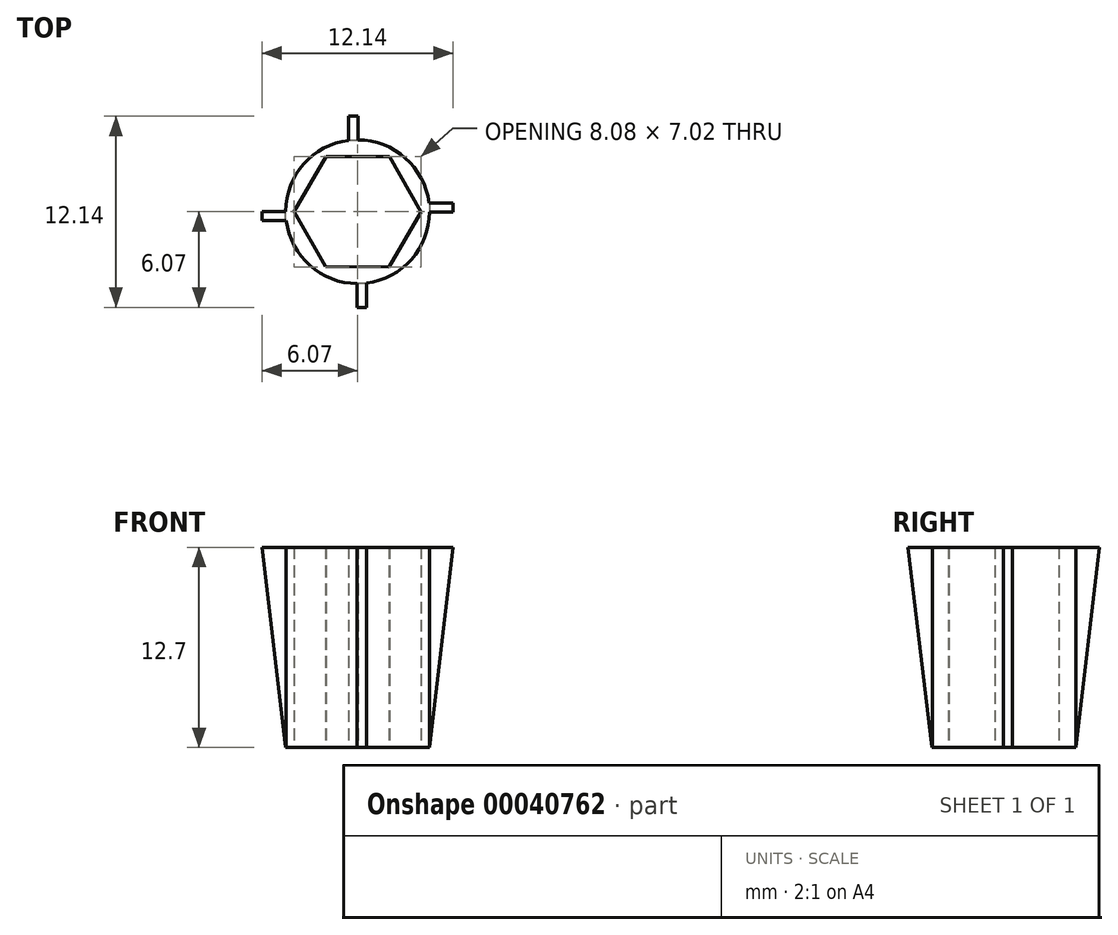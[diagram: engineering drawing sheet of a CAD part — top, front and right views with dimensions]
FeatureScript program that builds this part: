
annotation { "Feature Type Name" : "Feature", "Feature Type Description" : "" }
export const myFeature = defineFeature(function(context is Context, id is Id, definition is map)
    precondition{}
    {
        {
            var Q0;
            Q0=qCreatedBy(makeId("Top.planeOp"),FACE);
            var sketch = newSketch(context, id + "F0", { "sketchPlane" : qUnion([Q0])});
            skCircle(sketch, "E0.cCircle", {"center": v(0, 0) * mm, "radius": 3.5 * mm, "construction": true});
            skLineSegment(sketch, "E0.0", {"start": v(2.04, 3.5) * mm, "end": v(4.04, -0.02) * mm});
            skLineSegment(sketch, "E0.1", {"start": v(4.04, -0.02) * mm, "end": v(2, -3.5) * mm});
            skLineSegment(sketch, "E0.2", {"start": v(2, -3.5) * mm, "end": v(-2.04, -3.5) * mm});
            skLineSegment(sketch, "E0.3", {"start": v(-2.04, -3.5) * mm, "end": v(-4.04, 0.02) * mm});
            skLineSegment(sketch, "E0.4", {"start": v(-4.04, 0.02) * mm, "end": v(-2, 3.5) * mm});
            skLineSegment(sketch, "E0.5", {"start": v(-2, 3.5) * mm, "end": v(2.04, 3.5) * mm});
            skPoint(sketch, "E0.0.midPoint", {"position": v(3.04, 1.74) * mm});
            skLineSegment(sketch, "E1", {"start": v(-2, 3.5) * mm, "end": v(-2.04, -3.5) * mm, "construction": true});
            skCircle(sketch, "E2", {"center": v(0, 0) * mm, "radius": 4.57 * mm});
            skLineSegment(sketch, "E3.bottom", {"start": v(4.04, -0.02) * mm, "end": v(6.07, -0.02) * mm});
            skLineSegment(sketch, "E3.top", {"start": v(4.04, 0.56) * mm, "end": v(6.07, 0.56) * mm});
            skLineSegment(sketch, "E3.left", {"start": v(4.04, -0.02) * mm, "end": v(4.04, 0.56) * mm});
            skLineSegment(sketch, "E3.right", {"start": v(6.07, -0.02) * mm, "end": v(6.07, 0.56) * mm});
            skLineSegment(sketch, "E4.1.0", {"start": v(-0.56, 4.04) * mm, "end": v(-0.56, 6.07) * mm});
            skLineSegment(sketch, "E4.1.1", {"start": v(0.02, 6.07) * mm, "end": v(-0.56, 6.07) * mm});
            skLineSegment(sketch, "E4.1.2", {"start": v(0.02, 4.04) * mm, "end": v(0.02, 6.07) * mm});
            skLineSegment(sketch, "E4.1.3", {"start": v(0.02, 4.04) * mm, "end": v(-0.56, 4.04) * mm});
            skLineSegment(sketch, "E4.2.0", {"start": v(-4.04, -0.56) * mm, "end": v(-6.07, -0.56) * mm});
            skLineSegment(sketch, "E4.2.1", {"start": v(-6.07, 0.02) * mm, "end": v(-6.07, -0.56) * mm});
            skLineSegment(sketch, "E4.2.2", {"start": v(-4.04, 0.02) * mm, "end": v(-6.07, 0.02) * mm});
            skLineSegment(sketch, "E4.2.3", {"start": v(-4.04, 0.02) * mm, "end": v(-4.04, -0.56) * mm});
            skLineSegment(sketch, "E4.3.0", {"start": v(0.56, -4.04) * mm, "end": v(0.56, -6.07) * mm});
            skLineSegment(sketch, "E4.3.1", {"start": v(-0.02, -6.07) * mm, "end": v(0.56, -6.07) * mm});
            skLineSegment(sketch, "E4.3.2", {"start": v(-0.02, -4.04) * mm, "end": v(-0.02, -6.07) * mm});
            skLineSegment(sketch, "E4.3.3", {"start": v(-0.02, -4.04) * mm, "end": v(0.56, -4.04) * mm});
            skSolve(sketch);
        }
        {
            var Q0;
            Q0=makeQuery(id+"F0.imprint","IMPRINT",FACE,{"disambiguationData":[TD([[makeQuery(id+"F0.imprint","IMPRINT",EDGE,{"derivedFrom":sQuery(id+"F0.wireOp",EDGE,"E0.0")}),1.0]])]});
            var Q1;
            {var subQ0=sQuery(id+"F0.wireOp",EDGE,"E3.right");Q1=makeQuery(id+"F0.imprint","IMPRINT",FACE,{"disambiguationData":[TD([[makeQuery(id+"F0.imprint","IMPRINT",EDGE,{"derivedFrom":subQ0}),1.0]])]});}
            var Q2;
            {var subQ0=sQuery(id+"F0.wireOp",EDGE,"E3.left");Q2=makeQuery(id+"F0.imprint","IMPRINT",FACE,{"disambiguationData":[TD([[makeQuery(id+"F0.imprint","IMPRINT",EDGE,{"derivedFrom":subQ0}),-1.0]])]});}
            var Q3;
            {var subQ3=sQuery(id+"F0.wireOp",EDGE,"E4.1.1");Q3=makeQuery(id+"F0.imprint","IMPRINT",FACE,{"disambiguationData":[TD([[makeQuery(id+"F0.imprint","IMPRINT",EDGE,{"derivedFrom":subQ3}),1.0]])]});}
            var Q4;
            {var subQ0=sQuery(id+"F0.wireOp",EDGE,"E4.1.3");Q4=makeQuery(id+"F0.imprint","IMPRINT",FACE,{"disambiguationData":[TD([[makeQuery(id+"F0.imprint","IMPRINT",EDGE,{"derivedFrom":subQ0}),-1.0]])]});}
            var Q5;
            {var subQ3=sQuery(id+"F0.wireOp",EDGE,"E4.2.1");Q5=makeQuery(id+"F0.imprint","IMPRINT",FACE,{"disambiguationData":[TD([[makeQuery(id+"F0.imprint","IMPRINT",EDGE,{"derivedFrom":subQ3}),1.0]])]});}
            var Q6;
            {var subQ0=sQuery(id+"F0.wireOp",EDGE,"E4.2.3");Q6=makeQuery(id+"F0.imprint","IMPRINT",FACE,{"disambiguationData":[TD([[makeQuery(id+"F0.imprint","IMPRINT",EDGE,{"derivedFrom":subQ0}),-1.0]])]});}
            var Q7;
            {var subQ6=sQuery(id+"F0.wireOp",EDGE,"E0.1");Q7=makeQuery(id+"F0.imprint","IMPRINT",FACE,{"disambiguationData":[TD([[makeQuery(id+"F0.imprint","IMPRINT",EDGE,{"derivedFrom":subQ6}),1.0]])]});}
            var Q8;
            {var subQ0=sQuery(id+"F0.wireOp",EDGE,"E4.3.3");Q8=makeQuery(id+"F0.imprint","IMPRINT",FACE,{"disambiguationData":[TD([[makeQuery(id+"F0.imprint","IMPRINT",EDGE,{"derivedFrom":subQ0}),-1.0]])]});}
            var Q9;
            {var subQ3=sQuery(id+"F0.wireOp",EDGE,"E4.3.1");Q9=makeQuery(id+"F0.imprint","IMPRINT",FACE,{"disambiguationData":[TD([[makeQuery(id+"F0.imprint","IMPRINT",EDGE,{"derivedFrom":subQ3}),1.0]])]});}
            extrude(context, id + "F1", {"entities" : qUnion([Q0, Q1, Q2, Q3, Q4, Q5, Q6, Q7, Q8, Q9]), "depth" : 12.7 * mm});
        }
        {
            var Q0;
            Q0=makeQuery(id+"F1.opExtrude","SWEPT_FACE",FACE,{"disambiguationData":[OSD([sQuery(id+"F0.wireOp",EDGE,"E4.1.2")])]});
            var sketch = newSketch(context, id + "F2", { "sketchPlane" : qUnion([Q0])});
            skLineSegment(sketch, "E5", {"start": v(6.07, 12.7) * mm, "end": v(6.07, 0) * mm});
            skLineSegment(sketch, "E6", {"start": v(6.07, 0) * mm, "end": v(4.57, 0) * mm});
            skLineSegment(sketch, "E7", {"start": v(4.57, 0) * mm, "end": v(6.07, 12.7) * mm});
            skSolve(sketch);
        }
        {
            var Q0;
            Q0=makeQuery(id+"F2.imprint","IMPRINT",FACE,{"disambiguationData":[TD([[makeQuery(id+"F2.imprint","IMPRINT",EDGE,{"derivedFrom":sQuery(id+"F2.wireOp",EDGE,"E5")}),-1.0]])]});
            extrude(context, id + "F3", {"entities" : qUnion([Q0]), "operationType" : NewBodyOperationType.REMOVE, "oppositeDirection" : true, "depth" : 25.4 * mm});
        }
        {
            var Q0;
            Q0=makeQuery(id+"F1.opExtrude","SWEPT_FACE",FACE,{"disambiguationData":[OSD([sQuery(id+"F0.wireOp",EDGE,"E3.bottom")])]});
            var sketch = newSketch(context, id + "F4", { "sketchPlane" : qUnion([Q0])});
            skLineSegment(sketch, "E8", {"start": v(6.07, 12.7) * mm, "end": v(6.07, 0) * mm});
            skLineSegment(sketch, "E9", {"start": v(6.07, 0) * mm, "end": v(4.57, 0) * mm});
            skLineSegment(sketch, "E10", {"start": v(4.57, 0) * mm, "end": v(6.07, 12.7) * mm});
            skSolve(sketch);
        }
        {
            var Q0;
            Q0=makeQuery(id+"F4.imprint","IMPRINT",FACE,{"disambiguationData":[TD([[makeQuery(id+"F4.imprint","IMPRINT",EDGE,{"derivedFrom":sQuery(id+"F4.wireOp",EDGE,"E8")}),-1.0]])]});
            extrude(context, id + "F5", {"entities" : qUnion([Q0]), "operationType" : NewBodyOperationType.REMOVE, "oppositeDirection" : true, "depth" : 25.4 * mm});
        }
        {
            var Q0;
            Q0=makeQuery(id+"F1.opExtrude","SWEPT_FACE",FACE,{"disambiguationData":[OSD([sQuery(id+"F0.wireOp",EDGE,"E4.3.2")])]});
            var sketch = newSketch(context, id + "F6", { "sketchPlane" : qUnion([Q0])});
            skLineSegment(sketch, "E11", {"start": v(6.07, 12.7) * mm, "end": v(6.07, 0) * mm});
            skLineSegment(sketch, "E12", {"start": v(6.07, 0) * mm, "end": v(4.57, 0) * mm});
            skLineSegment(sketch, "E13", {"start": v(4.57, 0) * mm, "end": v(6.07, 12.7) * mm});
            skSolve(sketch);
        }
        {
            var Q0;
            Q0=makeQuery(id+"F6.imprint","IMPRINT",FACE,{"disambiguationData":[TD([[makeQuery(id+"F6.imprint","IMPRINT",EDGE,{"derivedFrom":sQuery(id+"F6.wireOp",EDGE,"E11")}),-1.0]])]});
            extrude(context, id + "F7", {"entities" : qUnion([Q0]), "operationType" : NewBodyOperationType.REMOVE, "oppositeDirection" : true, "depth" : 25.4 * mm});
        }
        {
            var Q0;
            Q0=makeQuery(id+"F1.opExtrude","SWEPT_FACE",FACE,{"disambiguationData":[OSD([sQuery(id+"F0.wireOp",EDGE,"E4.2.2")])]});
            var sketch = newSketch(context, id + "F8", { "sketchPlane" : qUnion([Q0])});
            skLineSegment(sketch, "E14", {"start": v(6.07, 12.7) * mm, "end": v(6.07, 0) * mm});
            skLineSegment(sketch, "E15", {"start": v(6.07, 0) * mm, "end": v(4.57, 0) * mm});
            skLineSegment(sketch, "E16", {"start": v(4.57, 0) * mm, "end": v(6.07, 12.7) * mm});
            skSolve(sketch);
        }
        {
            var Q0;
            Q0=makeQuery(id+"F8.imprint","IMPRINT",FACE,{"disambiguationData":[TD([[makeQuery(id+"F8.imprint","IMPRINT",EDGE,{"derivedFrom":sQuery(id+"F8.wireOp",EDGE,"E14")}),-1.0]])]});
            extrude(context, id + "F9", {"entities" : qUnion([Q0]), "operationType" : NewBodyOperationType.REMOVE, "oppositeDirection" : true, "depth" : 25.4 * mm});
        }
    });
